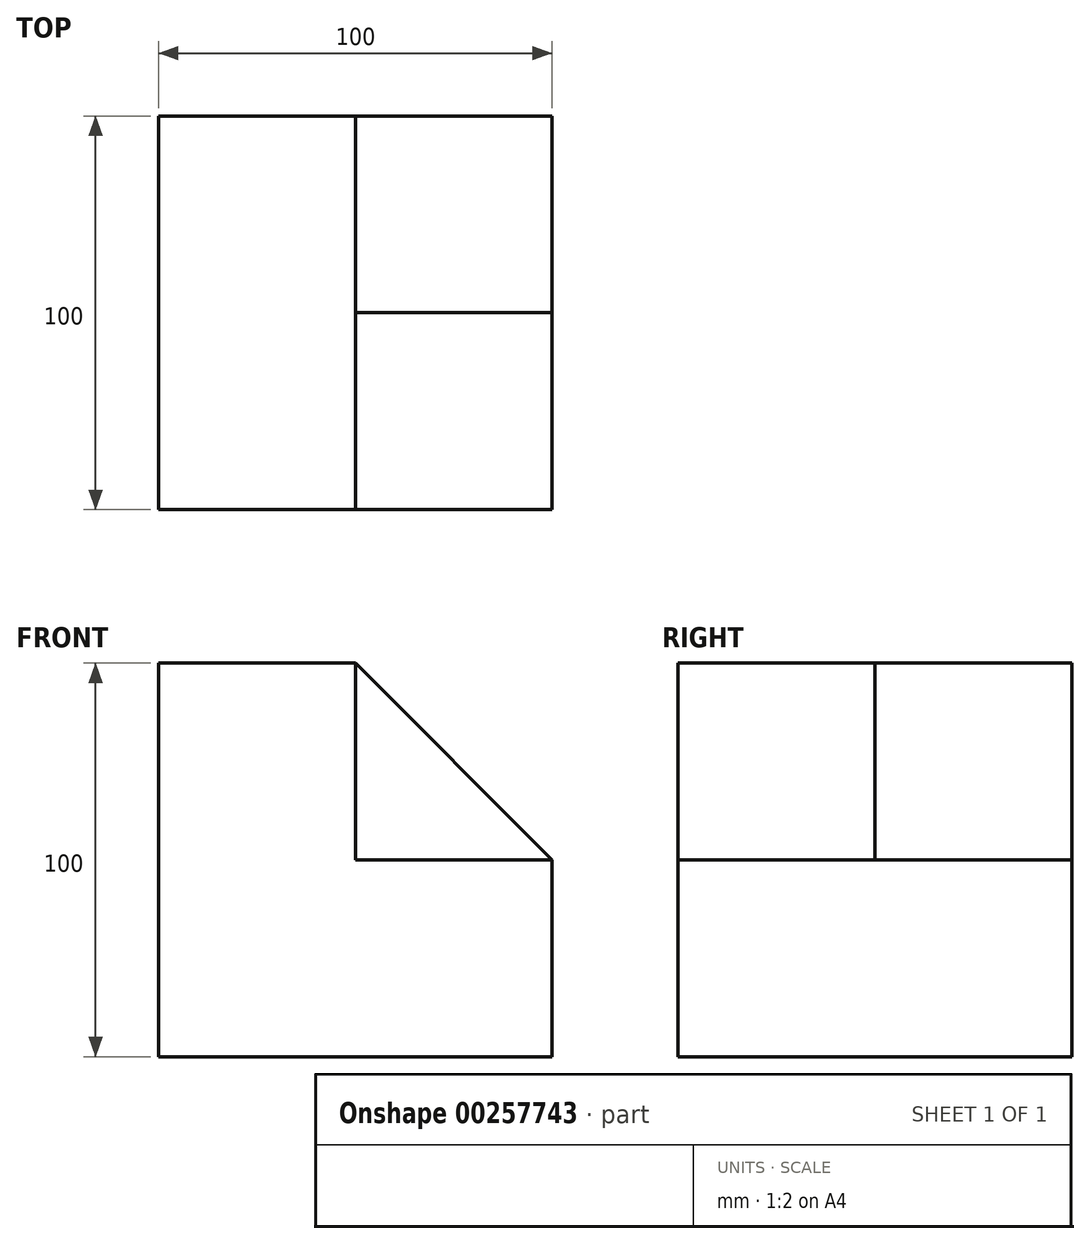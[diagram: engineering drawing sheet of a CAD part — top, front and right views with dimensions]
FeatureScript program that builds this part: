
annotation { "Feature Type Name" : "Feature", "Feature Type Description" : "" }
export const myFeature = defineFeature(function(context is Context, id is Id, definition is map)
    precondition{}
    {
        {
            var Q0;
            Q0=qCreatedBy(makeId("Front.planeOp"),FACE);
            var sketch = newSketch(context, id + "F0", { "sketchPlane" : qUnion([Q0])});
            skLineSegment(sketch, "E0", {"start": v(-100, 100) * mm, "end": v(-100, 0) * mm});
            skLineSegment(sketch, "E1", {"start": v(0, 0) * mm, "end": v(0, 50) * mm});
            skLineSegment(sketch, "E2", {"start": v(-50, 100) * mm, "end": v(-100, 100) * mm});
            skLineSegment(sketch, "E3", {"start": v(-100, 0) * mm, "end": v(0, 0) * mm});
            skLineSegment(sketch, "E4", {"start": v(-50, 100) * mm, "end": v(0, 50) * mm});
            skSolve(sketch);
        }
        {
            var Q0;
            Q0 = qSketchRegion(id + "F0", true);
            extrude(context, id + "F1", {"entities" : qUnion([Q0]), "depth" : 100 * mm});
        }
        {
            var Q0;
            Q0=makeQuery(id+"F1.opExtrude","CAP_FACE",FACE,{"disambiguationData":[OSD([sQuery(id+"F0.wireOp",EDGE,"E0"),sQuery(id+"F0.wireOp",EDGE,"E1"),sQuery(id+"F0.wireOp",EDGE,"E2"),sQuery(id+"F0.wireOp",EDGE,"E3"),sQuery(id+"F0.wireOp",EDGE,"E4")])],"isStart":false});
            var sketch = newSketch(context, id + "F2", { "sketchPlane" : qUnion([Q0])});
            skLineSegment(sketch, "E5", {"start": v(-50, 100) * mm, "end": v(-50, 50) * mm});
            skLineSegment(sketch, "E6", {"start": v(-50, 50) * mm, "end": v(0, 50) * mm});
            skLineSegment(sketch, "E7", {"start": v(-50, 100) * mm, "end": v(0, 50) * mm});
            skSolve(sketch);
        }
        {
            var Q0;
            Q0=makeQuery(id+"F2.imprint","IMPRINT",FACE,{"disambiguationData":[TD([[makeQuery(id+"F2.imprint","IMPRINT",EDGE,{"derivedFrom":sQuery(id+"F2.wireOp",EDGE,"E5")}),1.0]])]});
            extrude(context, id + "F3", {"entities" : qUnion([Q0]), "operationType" : NewBodyOperationType.REMOVE, "oppositeDirection" : true, "depth" : 50 * mm});
        }
    });
